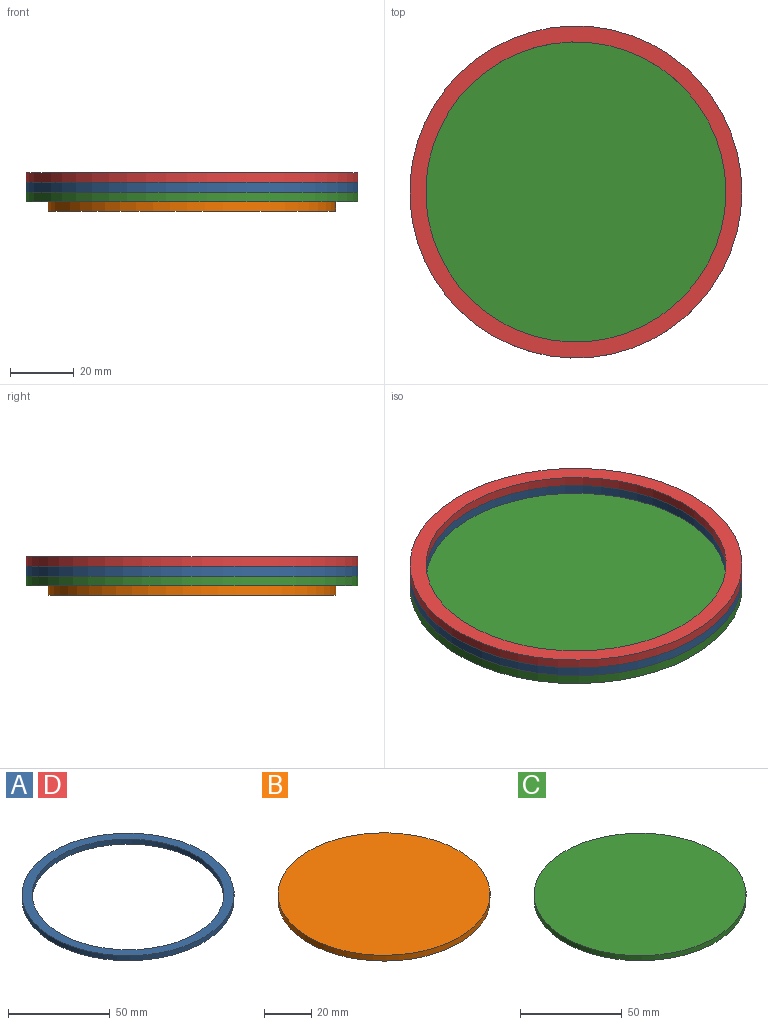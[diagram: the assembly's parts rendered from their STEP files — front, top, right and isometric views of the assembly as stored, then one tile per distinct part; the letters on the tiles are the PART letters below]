
ASSEMBLY  parts=4 mates=2
PART A: 4 faces, bbox 104x104x3 mm
  f0: cylinder r=47mm len=94mm, axis (0,0,-1), area 885.9mm2, adj f2,f3
  f1: cylinder r=52mm len=104mm, axis (0,0,-1), area 980.2mm2, adj f2,f3
  f2: plane 104x104mm, normal (0,0,1), area 1555.1mm2, adj f0,f1
  f3: plane 104x104mm, normal (0,0,-1), area 1555.1mm2, adj f0,f1
PART B: 3 faces, bbox 90x90x3 mm
  f0: cylinder r=45mm len=90mm, axis (0,0,-1), area 848.2mm2, adj f1,f2
  f1: plane 90x90mm, normal (0,0,1), area 6361.7mm2, adj f0
  f2: plane 90x90mm, normal (0,0,-1), area 6361.7mm2, adj f0
PART C: 3 faces, bbox 104x104x3 mm
  f0: cylinder r=52mm len=104mm, axis (0,0,-1), area 980.2mm2, adj f1,f2
  f1: plane 104x104mm, normal (0,0,1), area 8494.9mm2, adj f0
  f2: plane 104x104mm, normal (0,0,-1), area 8494.9mm2, adj f0
PART D: same geometry as A
PLACE A at identity
PLACE B t=(0,0,-6)mm
PLACE C t=(0,0,-3)mm
PLACE D t=(0,0,3)mm
MATE fastened B.f0 <-> C.f0  axis (0,0,1) through (0,0,-3)mm
MATE fastened D.f1 <-> A.f1  axis (0,0,-1) through (0,0,3)mm
